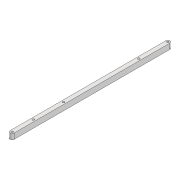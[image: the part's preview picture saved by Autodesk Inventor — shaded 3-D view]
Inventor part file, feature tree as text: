
AUTODESK INVENTOR PART (.ipt)
format: ipt  version: 2022 (Build 260153000, 153)  size: 95,232 bytes
history: native  units: mm
features: extrude x1, sketch x1
ambient origin geometry x8: Origin, YZ Plane, XZ Plane, XY Plane, X Axis, Y Axis, Z Axis, Center Point
bodies: Solid1 (feature_tree)
feature tree (2):
  extrude  "Extrusion1"  Depth=6.0mm
  sketch  "Sketch1"  dims[d0=226.421mm d1=6.0mm d2=3.0mm d3=3.0mm d4=8.0mm d5=0.0mm d6=3.0mm d7=184.147mm d8=3.0mm d9=74.612mm d10=3.0mm d11=30.851mm]
